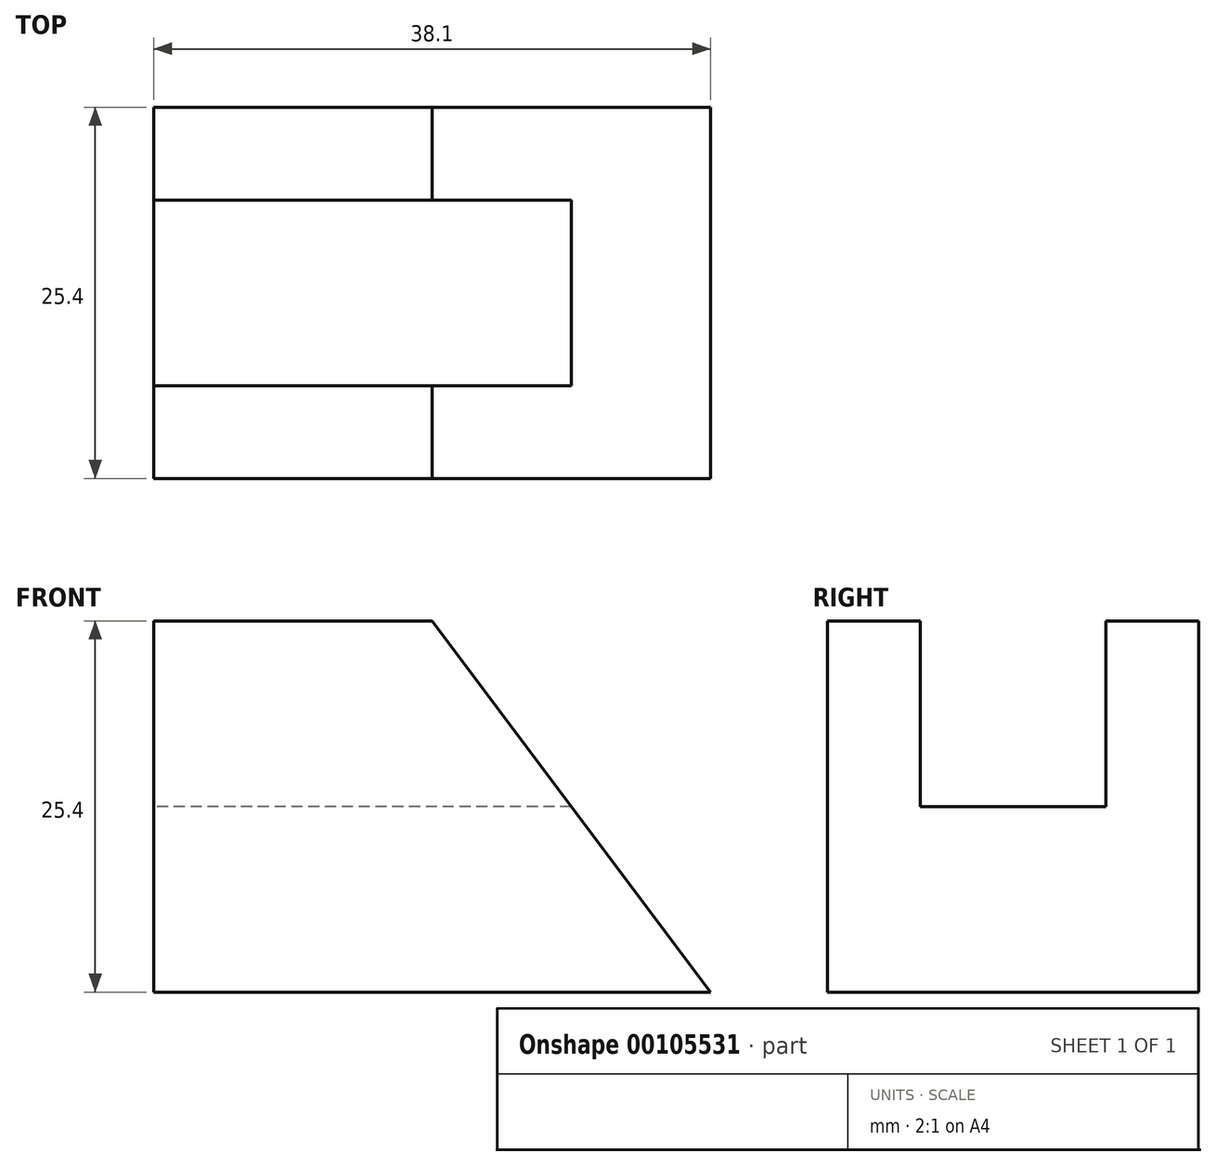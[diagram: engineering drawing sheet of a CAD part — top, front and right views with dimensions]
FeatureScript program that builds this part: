
annotation { "Feature Type Name" : "Feature", "Feature Type Description" : "" }
export const myFeature = defineFeature(function(context is Context, id is Id, definition is map)
    precondition{}
    {
        {
            var Q0;
            Q0=qCreatedBy(makeId("Right.planeOp"),FACE);
            var sketch = newSketch(context, id + "F0", { "sketchPlane" : qUnion([Q0])});
            skLineSegment(sketch, "E0", {"start": v(0, 0) * mm, "end": v(0, 25.4) * mm});
            skLineSegment(sketch, "E1", {"start": v(0, 25.4) * mm, "end": v(6.35, 25.4) * mm});
            skLineSegment(sketch, "E2", {"start": v(6.35, 25.4) * mm, "end": v(6.35, 12.7) * mm});
            skLineSegment(sketch, "E3", {"start": v(6.35, 12.7) * mm, "end": v(19.05, 12.7) * mm});
            skLineSegment(sketch, "E4", {"start": v(19.05, 12.7) * mm, "end": v(19.05, 25.4) * mm});
            skLineSegment(sketch, "E5", {"start": v(19.05, 25.4) * mm, "end": v(25.4, 25.4) * mm});
            skLineSegment(sketch, "E6", {"start": v(25.4, 25.4) * mm, "end": v(25.4, 0) * mm});
            skLineSegment(sketch, "E7", {"start": v(25.4, 0) * mm, "end": v(0, 0) * mm});
            skSolve(sketch);
        }
        {
            var Q0;
            Q0=makeQuery(id+"F0.imprint","IMPRINT",FACE,{"disambiguationData":[TD([[makeQuery(id+"F0.imprint","IMPRINT",EDGE,{"derivedFrom":sQuery(id+"F0.wireOp",EDGE,"E0")}),-1.0]])]});
            extrude(context, id + "F1", {"entities" : qUnion([Q0]), "depth" : 38.1 * mm});
        }
        {
            var Q0;
            Q0=qCreatedBy(makeId("Front.planeOp"),FACE);
            var sketch = newSketch(context, id + "F2", { "sketchPlane" : qUnion([Q0])});
            skLineSegment(sketch, "E8", {"start": v(0, 0) * mm, "end": v(38.1, 0) * mm});
            skLineSegment(sketch, "E9", {"start": v(38.1, 0) * mm, "end": v(19.05, 25.4) * mm});
            skLineSegment(sketch, "E10", {"start": v(19.05, 25.4) * mm, "end": v(0, 25.4) * mm});
            skLineSegment(sketch, "E11", {"start": v(0, 25.4) * mm, "end": v(0, 0) * mm});
            skSolve(sketch);
        }
        {
            var Q0;
            Q0 = qSketchRegion(id + "F2", true);
            extrude(context, id + "F3", {"entities" : qUnion([Q0]), "operationType" : NewBodyOperationType.INTERSECT, "oppositeDirection" : true, "depth" : 25.4 * mm});
        }
    });
